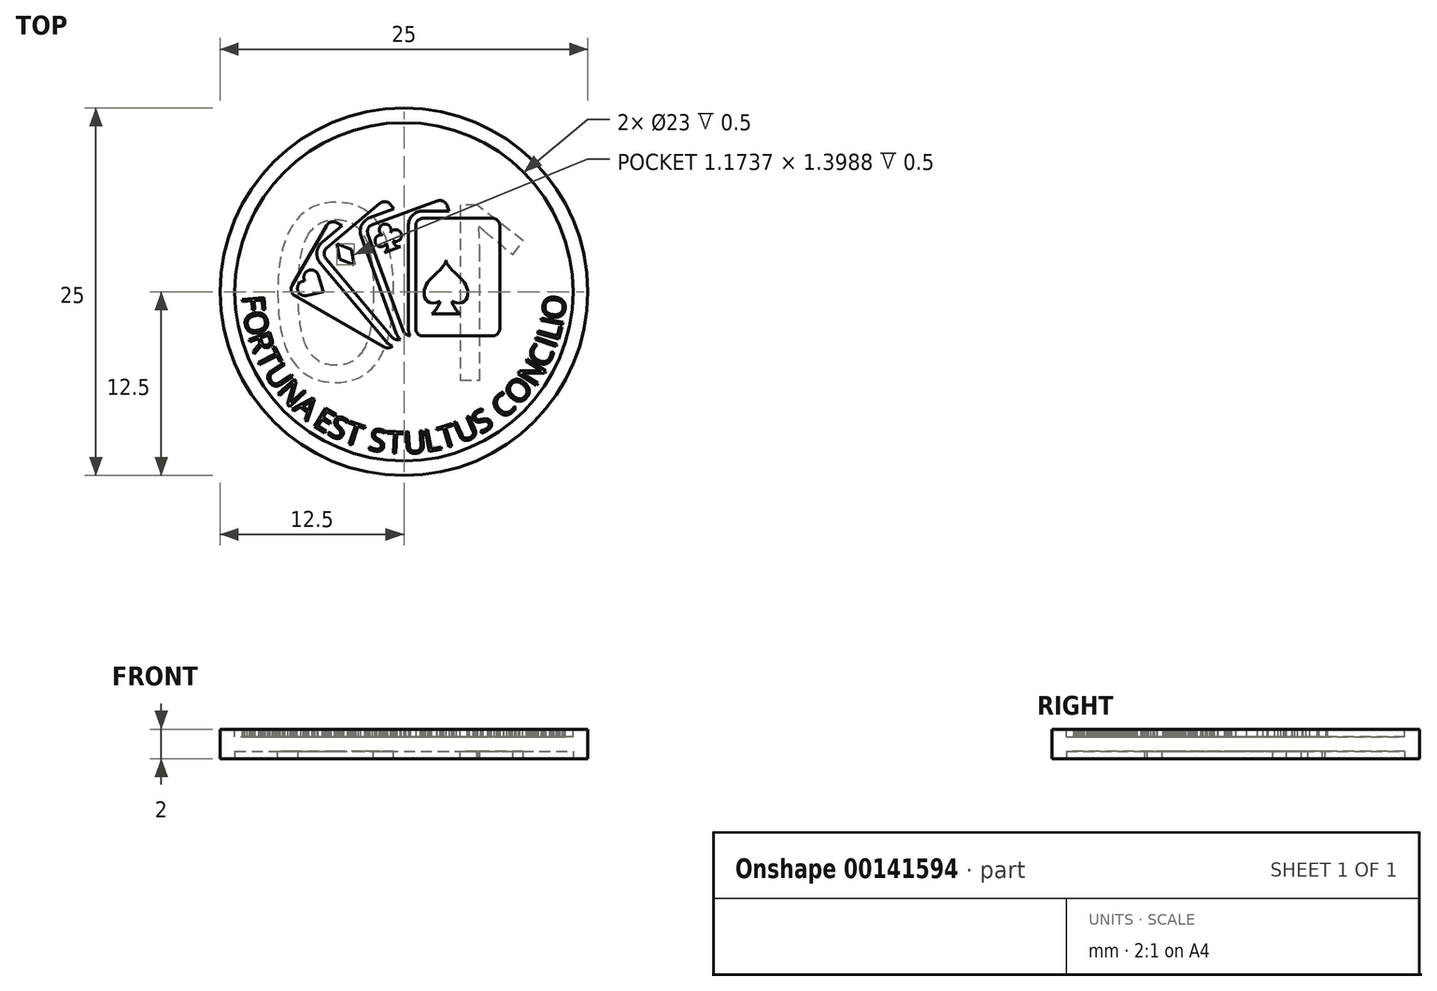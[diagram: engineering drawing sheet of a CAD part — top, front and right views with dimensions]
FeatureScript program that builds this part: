
annotation { "Feature Type Name" : "Feature", "Feature Type Description" : "" }
export const myFeature = defineFeature(function(context is Context, id is Id, definition is map)
    precondition{}
    {
        {
            assignVariable(context, id + "F0", {"name" : "ImpressionDepth", "anyValue" : 0.5});
        }
        {
            var Q0;
            Q0=qCreatedBy(makeId("Top.planeOp"),FACE);
            var sketch = newSketch(context, id + "F1", { "sketchPlane" : qUnion([Q0])});
            skCircle(sketch, "E0", {"center": v(0, 0) * mm, "radius": 12.5 * mm});
            skSolve(sketch);
        }
        {
            var Q0;
            Q0=qSketchRegion(id+"F1",true);
            extrude(context, id + "F2", {"entities" : qUnion([Q0]), "depth" : 2 * mm});
        }
        {
            var Q0;
            Q0=makeQuery(id+"F2.opExtrude","CAP_FACE",FACE,{"disambiguationData":[OSD([sQuery(id+"F1.wireOp",EDGE,"E0")])],"isStart":false});
            var sketch = newSketch(context, id + "F3", { "sketchPlane" : qUnion([Q0])});
            skCircle(sketch, "E1.0", {"center": v(0, 0) * mm, "radius": 11.5 * mm});
            skSolve(sketch);
        }
        {
            var Q0;
            Q0=qSketchRegion(id+"F3",true);
            extrude(context, id + "F4", {"entities" : qUnion([Q0]), "operationType" : NewBodyOperationType.REMOVE, "oppositeDirection" : true, "depth" : (getVariable(context, 'ImpressionDepth')) * mm});
        }
        {
            var Q0;
            Q0=makeQuery(id+"F2.opExtrude","CAP_FACE",FACE,{"disambiguationData":[OSD([sQuery(id+"F1.wireOp",EDGE,"E0")])],"isStart":true});
            var sketch = newSketch(context, id + "F5", { "sketchPlane" : qUnion([Q0])});
            skCircle(sketch, "E2.0", {"center": v(0, 0) * mm, "radius": 11.5 * mm});
            skSolve(sketch);
        }
        {
            var Q0;
            Q0=qSketchRegion(id+"F5",true);
            extrude(context, id + "F6", {"entities" : qUnion([Q0]), "operationType" : NewBodyOperationType.REMOVE, "oppositeDirection" : true, "depth" : (getVariable(context, 'ImpressionDepth')) * mm});
        }
        {
            var Q0;
            Q0=makeQuery(id+"F6.boolean.opBoolean","COPY",FACE,{"derivedFrom":makeQuery(id+"F6.opExtrude","CAP_FACE",FACE,{"disambiguationData":[OSD([sQuery(id+"F5.wireOp",EDGE,"E2.0")])],"isStart":false})});
            var sketch = newSketch(context, id + "F7", { "sketchPlane" : qUnion([Q0])});
            skText(sketch, "E3", { "text": "10", "fontName": "OpenSans-Regular.ttf"});
            skPoint(sketch, "E4", {"position": v(0, 0) * mm});
            const initialGuessF7  = {"E3": [0.00965, 0.006, -1, 0, 0.012]};
            skSetInitialGuess(sketch, initialGuessF7);
            skSolve(sketch);
        }
        {
            var Q0;
            Q0 = qSketchRegion(id + "F7", true);
            extrude(context, id + "F8", {"entities" : qUnion([Q0]), "operationType" : NewBodyOperationType.ADD, "depth" : (getVariable(context, 'ImpressionDepth')) * mm});
        }
        {
            var Q0;
            Q0=makeQuery(id+"F4.boolean.opBoolean","COPY",FACE,{"derivedFrom":makeQuery(id+"F4.opExtrude","CAP_FACE",FACE,{"disambiguationData":[OSD([sQuery(id+"F3.wireOp",EDGE,"E1.0")])],"isStart":false})});
            var sketch = newSketch(context, id + "F9", { "sketchPlane" : qUnion([Q0])});
            skLineSegment(sketch, "E5.bottom", {"start": v(1.3, 5) * mm, "end": v(6.01, 5) * mm});
            skLineSegment(sketch, "E5.top", {"start": v(1.3, -3) * mm, "end": v(6.01, -3) * mm});
            skLineSegment(sketch, "E5.left", {"start": v(0.8, 4.5) * mm, "end": v(0.8, -2.5) * mm});
            skLineSegment(sketch, "E5.right", {"start": v(6.51, 4.5) * mm, "end": v(6.51, -2.5) * mm});
            skPoint(sketch, "E6.visualSharp", {"position": v(0.8, 5) * mm});
            skArc(sketch, "E6.filletArc", {"start": v(1.3, 5) * mm, "mid": v(0.95, 4.85) * mm, "end": v(0.8, 4.5) * mm});
            skPoint(sketch, "E7.visualSharp", {"position": v(6.51, 5) * mm});
            skArc(sketch, "E7.filletArc", {"start": v(6.51, 4.5) * mm, "mid": v(6.37, 4.85) * mm, "end": v(6.01, 5) * mm});
            skPoint(sketch, "E8.visualSharp", {"position": v(0.8, -3) * mm});
            skArc(sketch, "E8.filletArc", {"start": v(0.8, -2.5) * mm, "mid": v(0.95, -2.85) * mm, "end": v(1.3, -3) * mm});
            skPoint(sketch, "E9.visualSharp", {"position": v(6.51, -3) * mm});
            skArc(sketch, "E9.filletArc", {"start": v(6.01, -3) * mm, "mid": v(6.37, -2.85) * mm, "end": v(6.51, -2.5) * mm});
            skPoint(sketch, "E10", {"position": v(0.8, -5) * mm});
            skLineSegment(sketch, "E11.bottom", {"start": v(-2.15, 4.57) * mm, "end": v(2.28, 6.18) * mm});
            skLineSegment(sketch, "E11.left", {"start": v(-2.45, 3.93) * mm, "end": v(-0.06, -2.65) * mm});
            skLineSegment(sketch, "E11.right", {"start": v(2.92, 5.88) * mm, "end": v(3.06, 5.5) * mm});
            skPoint(sketch, "E12.visualSharp", {"position": v(-2.62, 4.4) * mm});
            skArc(sketch, "E12.filletArc", {"start": v(-2.15, 4.57) * mm, "mid": v(-2.43, 4.3) * mm, "end": v(-2.45, 3.93) * mm});
            skPoint(sketch, "E13.visualSharp", {"position": v(2.75, 6.35) * mm});
            skArc(sketch, "E13.filletArc", {"start": v(2.92, 5.88) * mm, "mid": v(2.66, 6.16) * mm, "end": v(2.28, 6.18) * mm});
            skPoint(sketch, "E14.visualSharp", {"position": v(0.12, -3.12) * mm});
            skArc(sketch, "E14.filletArc", {"start": v(-0.06, -2.65) * mm, "mid": v(0.13, -2.9) * mm, "end": v(0.42, -2.98) * mm});
            skLineSegment(sketch, "E15", {"start": v(0.8, -5) * mm, "end": v(-2.62, 4.4) * mm, "construction": true});
            skLineSegment(sketch, "E16", {"start": v(0.8, -3) * mm, "end": v(0.8, -5) * mm, "construction": true});
            skLineSegment(sketch, "E17", {"start": v(1.3, 5) * mm, "end": v(3.24, 5) * mm});
            skArc(sketch, "E18.0", {"start": v(0.3, -2.5) * mm, "mid": v(0.33, -2.75) * mm, "end": v(0.42, -2.98) * mm});
            skLineSegment(sketch, "E18.1", {"start": v(0.3, 4.5) * mm, "end": v(0.3, -2.5) * mm});
            skArc(sketch, "E18.2", {"start": v(1.3, 5.5) * mm, "mid": v(0.6, 5.2) * mm, "end": v(0.3, 4.5) * mm});
            skLineSegment(sketch, "E18.3", {"start": v(1.3, 5.5) * mm, "end": v(3.06, 5.5) * mm});
            skLineSegment(sketch, "E19", {"start": v(-0.06, -2.65) * mm, "end": v(0.41, -2.48) * mm, "construction": true});
            skLineSegment(sketch, "E20", {"start": v(0.42, -2.98) * mm, "end": v(0.41, -2.48) * mm, "construction": true});
            skLineSegment(sketch, "E21.bottom", {"start": v(-5.24, 2.98) * mm, "end": v(-1.63, 6.01) * mm});
            skLineSegment(sketch, "E21.left", {"start": v(-5.3, 2.28) * mm, "end": v(-0.8, -3.08) * mm});
            skLineSegment(sketch, "E21.right", {"start": v(-0.93, 5.95) * mm, "end": v(-0.67, 5.64) * mm});
            skPoint(sketch, "E22.visualSharp", {"position": v(-5.63, 2.66) * mm});
            skArc(sketch, "E22.filletArc", {"start": v(-5.24, 2.98) * mm, "mid": v(-5.42, 2.64) * mm, "end": v(-5.3, 2.28) * mm});
            skPoint(sketch, "E23.visualSharp", {"position": v(-1.25, 6.33) * mm});
            skArc(sketch, "E23.filletArc", {"start": v(-0.93, 5.95) * mm, "mid": v(-1.27, 6.13) * mm, "end": v(-1.63, 6.01) * mm});
            skPoint(sketch, "E24.visualSharp", {"position": v(-0.49, -3.47) * mm});
            skArc(sketch, "E24.filletArc", {"start": v(-0.8, -3.08) * mm, "mid": v(-0.55, -3.25) * mm, "end": v(-0.25, -3.23) * mm});
            skLineSegment(sketch, "E25", {"start": v(-0.49, -3.47) * mm, "end": v(0.8, -5) * mm, "construction": true});
            skLineSegment(sketch, "E26", {"start": v(-5.24, 2.98) * mm, "end": v(-2.54, 5.26) * mm});
            skArc(sketch, "E27.0", {"start": v(-0.52, -2.82) * mm, "mid": v(-0.41, -3.04) * mm, "end": v(-0.25, -3.23) * mm});
            skLineSegment(sketch, "E27.1", {"start": v(-2.92, 3.76) * mm, "end": v(-0.52, -2.82) * mm});
            skArc(sketch, "E27.2", {"start": v(-2.32, 5.04) * mm, "mid": v(-2.89, 4.52) * mm, "end": v(-2.92, 3.76) * mm});
            skLineSegment(sketch, "E27.3", {"start": v(-2.32, 5.04) * mm, "end": v(-0.67, 5.64) * mm});
            skLineSegment(sketch, "E28", {"start": v(-0.8, -3.08) * mm, "end": v(-0.42, -2.76) * mm, "construction": true});
            skLineSegment(sketch, "E29", {"start": v(-0.25, -3.23) * mm, "end": v(-0.42, -2.76) * mm, "construction": true});
            skLineSegment(sketch, "E30.bottom", {"start": v(-7.61, 0.43) * mm, "end": v(-5.25, 4.52) * mm});
            skLineSegment(sketch, "E30.top", {"start": v(-0.4, -3.07) * mm, "end": v(-0.34, -2.98) * mm});
            skLineSegment(sketch, "E30.left", {"start": v(-7.43, -0.25) * mm, "end": v(-1.37, -3.75) * mm});
            skLineSegment(sketch, "E30.right", {"start": v(-4.57, 4.7) * mm, "end": v(-4.22, 4.5) * mm});
            skPoint(sketch, "E31.visualSharp", {"position": v(-7.86, 0) * mm});
            skArc(sketch, "E31.filletArc", {"start": v(-7.61, 0.43) * mm, "mid": v(-7.66, 0.05) * mm, "end": v(-7.43, -0.25) * mm});
            skPoint(sketch, "E32.visualSharp", {"position": v(-5, 4.95) * mm});
            skArc(sketch, "E32.filletArc", {"start": v(-4.57, 4.7) * mm, "mid": v(-4.95, 4.75) * mm, "end": v(-5.25, 4.52) * mm});
            skPoint(sketch, "E33.visualSharp", {"position": v(-0.93, -4) * mm});
            skArc(sketch, "E33.filletArc", {"start": v(-1.37, -3.75) * mm, "mid": v(-1.07, -3.81) * mm, "end": v(-0.79, -3.7) * mm});
            skPoint(sketch, "E34.visualSharp", {"position": v(1.93, 0.95) * mm});
            skLineSegment(sketch, "E35", {"start": v(-0.93, -4) * mm, "end": v(0.8, -5) * mm, "construction": true});
            skLineSegment(sketch, "E36", {"start": v(-7.61, 0.43) * mm, "end": v(-5.67, 3.8) * mm});
            skLineSegment(sketch, "E37.0", {"start": v(-5.57, 3.36) * mm, "end": v(-4.22, 4.5) * mm});
            skArc(sketch, "E37.1", {"start": v(-5.57, 3.36) * mm, "mid": v(-5.92, 2.69) * mm, "end": v(-5.69, 1.96) * mm});
            skLineSegment(sketch, "E37.2", {"start": v(-5.69, 1.96) * mm, "end": v(-1.19, -3.4) * mm});
            skArc(sketch, "E37.3", {"start": v(-1.19, -3.4) * mm, "mid": v(-1, -3.58) * mm, "end": v(-0.79, -3.7) * mm});
            skSolve(sketch);
        }
        {
            var Q0;
            Q0 = qSketchRegion(id + "F9", true);
            extrude(context, id + "F10", {"entities" : qUnion([Q0]), "operationType" : NewBodyOperationType.ADD, "depth" : (getVariable(context, 'ImpressionDepth')) * mm});
        }
        {
            var Q0;
            Q0=makeQuery(id+"F10.opExtrude","CAP_FACE",FACE,{"disambiguationData":[OSD([sQuery(id+"F9.wireOp",EDGE,"E5.bottom"),sQuery(id+"F9.wireOp",EDGE,"E5.top"),sQuery(id+"F9.wireOp",EDGE,"E5.right"),sQuery(id+"F9.wireOp",EDGE,"E6.filletArc"),sQuery(id+"F9.wireOp",EDGE,"E7.filletArc"),sQuery(id+"F9.wireOp",EDGE,"E8.filletArc"),sQuery(id+"F9.wireOp",EDGE,"E9.filletArc"),sQuery(id+"F9.wireOp",EDGE,"E17"),sQuery(id+"F9.wireOp",EDGE,"E5.left")])],"isStart":false});
            var sketch = newSketch(context, id + "F11", { "sketchPlane" : qUnion([Q0])});
            skLineSegment(sketch, "E38", {"start": v(2.86, 5) * mm, "end": v(2.86, -3) * mm, "construction": true});
            skLineSegment(sketch, "E39", {"start": v(0.8, 0) * mm, "end": v(6.51, 0) * mm, "construction": true});
            skLineSegment(sketch, "E40", {"start": v(2.86, -1.5) * mm, "end": v(3.82, -1.5) * mm});
            skPoint(sketch, "E41", {"position": v(3.26, -0.64) * mm});
            skPoint(sketch, "E42", {"position": v(4.73, -0.3) * mm});
            skArc(sketch, "E43", {"start": v(3.26, -0.64) * mm, "mid": v(3.46, -1.12) * mm, "end": v(3.82, -1.5) * mm});
            skPoint(sketch, "E44", {"position": v(2.86, 2.16) * mm});
            skPoint(sketch, "E45", {"position": v(3.36, 1.4) * mm});
            skPoint(sketch, "E46", {"position": v(4.16, 0.53) * mm});
            skFitSpline(sketch, "E47", {"points": [v(3.26, -0.64) * mm, v(4.29, -0.43) * mm, v(4.16, 0.53) * mm, v(3.36, 1.4) * mm, v(2.86, 2.16) * mm], "startDerivative": vector(6.48, -2.91) * mm, "endDerivative": vector(0, 2.74) * mm});
            skFitSpline(sketch, "E48.MirrorCS", {"points": [v(2.46, -0.64) * mm, v(1.43, -0.43) * mm, v(1.56, 0.53) * mm, v(2.36, 1.4) * mm, v(2.86, 2.16) * mm], "startDerivative": vector(-6.48, -2.91) * mm, "endDerivative": vector(0, 2.74) * mm});
            skArc(sketch, "E49.MirrorCS", {"start": v(2.46, -0.64) * mm, "mid": v(2.25, -1.12) * mm, "end": v(1.9, -1.5) * mm});
            skLineSegment(sketch, "E50.MirrorCS", {"start": v(2.86, -1.5) * mm, "end": v(1.9, -1.5) * mm});
            skLineSegment(sketch, "E51", {"start": v(-2.14, 3.08) * mm, "end": v(-1.01, 3.5) * mm, "construction": true});
            skLineSegment(sketch, "E52", {"start": v(-1.01, 3.5) * mm, "end": v(-1.5, 4.8) * mm, "construction": true});
            skLineSegment(sketch, "E53", {"start": v(-1.01, 3.5) * mm, "end": v(-0.53, 2.18) * mm, "construction": true});
            skLineSegment(sketch, "E54", {"start": v(-0.79, 2.87) * mm, "end": v(-0.25, 3.06) * mm});
            skPoint(sketch, "E55", {"position": v(-0.73, 3.46) * mm});
            skPoint(sketch, "E56", {"position": v(-1.27, 4.2) * mm});
            skPoint(sketch, "E57", {"position": v(-0.57, 3.83) * mm});
            skPoint(sketch, "E58", {"position": v(-0.29, 3.5) * mm});
            skArc(sketch, "E59", {"start": v(-0.73, 3.46) * mm, "mid": v(-0.57, 3.16) * mm, "end": v(-0.25, 3.06) * mm});
            skArc(sketch, "E60", {"start": v(-0.73, 3.46) * mm, "mid": v(-0.19, 3.95) * mm, "end": v(-0.91, 4.04) * mm});
            skArc(sketch, "E61", {"start": v(-1.41, 4.58) * mm, "mid": v(-0.98, 4.48) * mm, "end": v(-0.91, 4.04) * mm});
            skArc(sketch, "E62.MirrorCS", {"start": v(-1.41, 4.58) * mm, "mid": v(-1.67, 4.22) * mm, "end": v(-1.44, 3.84) * mm});
            skArc(sketch, "E63.MirrorCS", {"start": v(-1.2, 3.29) * mm, "mid": v(-1.94, 3.3) * mm, "end": v(-1.44, 3.84) * mm});
            skArc(sketch, "E64.MirrorCS", {"start": v(-1.2, 3.29) * mm, "mid": v(-1.14, 2.96) * mm, "end": v(-1.32, 2.67) * mm});
            skLineSegment(sketch, "E65.MirrorCS", {"start": v(-0.79, 2.87) * mm, "end": v(-1.32, 2.67) * mm});
            skLineSegment(sketch, "E66", {"start": v(-4.89, 1.78) * mm, "end": v(-3.97, 2.55) * mm, "construction": true});
            skLineSegment(sketch, "E67", {"start": v(-3.97, 2.55) * mm, "end": v(-4.7, 3.43) * mm, "construction": true});
            skLineSegment(sketch, "E68", {"start": v(-4.35, 2.23) * mm, "end": v(-4.55, 3.25) * mm});
            skLineSegment(sketch, "E69", {"start": v(-3.97, 2.55) * mm, "end": v(-3.38, 1.85) * mm, "construction": true});
            skLineSegment(sketch, "E70", {"start": v(-4.35, 2.23) * mm, "end": v(-3.38, 1.85) * mm});
            skLineSegment(sketch, "E71.MirrorCS", {"start": v(-3.58, 2.87) * mm, "end": v(-4.55, 3.25) * mm});
            skLineSegment(sketch, "E72.MirrorCS", {"start": v(-3.58, 2.87) * mm, "end": v(-3.38, 1.85) * mm});
            skLineSegment(sketch, "E73", {"start": v(-6.86, -0.58) * mm, "end": v(-6.26, 0.46) * mm, "construction": true});
            skLineSegment(sketch, "E74", {"start": v(-6.26, 0.46) * mm, "end": v(-7.26, 1.04) * mm, "construction": true});
            skLineSegment(sketch, "E75", {"start": v(-6.26, 0.46) * mm, "end": v(-5.47, 0) * mm, "construction": true});
            skLineSegment(sketch, "E76", {"start": v(-5.47, 0) * mm, "end": v(-5.83, 1.14) * mm});
            skArc(sketch, "E77", {"start": v(-5.83, 1.14) * mm, "mid": v(-6.5, 1.45) * mm, "end": v(-6.74, 0.74) * mm});
            skArc(sketch, "E78.MirrorCS", {"start": v(-6.63, -0.25) * mm, "mid": v(-7.24, 0.19) * mm, "end": v(-6.74, 0.74) * mm});
            skLineSegment(sketch, "E79.MirrorCS", {"start": v(-5.47, 0) * mm, "end": v(-6.63, -0.25) * mm});
            skSolve(sketch);
        }
        {
            var Q0;
            Q0 = qSketchRegion(id + "F11", true);
            extrude(context, id + "F12", {"entities" : qUnion([Q0]), "operationType" : NewBodyOperationType.REMOVE, "oppositeDirection" : true, "depth" : (getVariable(context, 'ImpressionDepth')) * mm});
        }
        {
            var Q0;
            Q0=makeQuery(id+"F4.boolean.opBoolean","COPY",FACE,{"derivedFrom":makeQuery(id+"F4.opExtrude","CAP_FACE",FACE,{"disambiguationData":[OSD([sQuery(id+"F3.wireOp",EDGE,"E1.0")])],"isStart":false})});
            var sketch = newSketch(context, id + "F13", { "sketchPlane" : qUnion([Q0])});
            skCircle(sketch, "E80", {"center": v(0, 0) * mm, "radius": 11 * mm, "construction": true});
            skLineSegment(sketch, "E81", {"start": v(0, 0) * mm, "end": v(0, -11) * mm, "construction": true});
            skText(sketch, "E82", { "text": "U", "fontName": "OpenSans-Regular.ttf"});
            skText(sketch, "E83", { "text": "L\n", "fontName": "OpenSans-Regular.ttf"});
            skText(sketch, "E84", { "text": "T", "fontName": "OpenSans-Regular.ttf"});
            skText(sketch, "E85", { "text": "U", "fontName": "OpenSans-Regular.ttf"});
            skText(sketch, "E86", { "text": "S", "fontName": "OpenSans-Regular.ttf"});
            skText(sketch, "E87", { "text": "C", "fontName": "OpenSans-Regular.ttf"});
            skText(sketch, "E88", { "text": "O", "fontName": "OpenSans-Regular.ttf"});
            skText(sketch, "E89", { "text": "N", "fontName": "OpenSans-Regular.ttf"});
            skText(sketch, "E90", { "text": "C", "fontName": "OpenSans-Regular.ttf"});
            skText(sketch, "E91", { "text": "O", "fontName": "OpenSans-Regular.ttf"});
            skText(sketch, "E92", { "text": "I", "fontName": "OpenSans-Regular.ttf"});
            skText(sketch, "E93", { "text": "L", "fontName": "OpenSans-Regular.ttf"});
            skText(sketch, "E94", { "text": "I", "fontName": "OpenSans-Regular.ttf"});
            skText(sketch, "E95", { "text": "F", "fontName": "OpenSans-Regular.ttf"});
            skText(sketch, "E96", { "text": "O", "fontName": "OpenSans-Regular.ttf"});
            skText(sketch, "E97", { "text": "R", "fontName": "OpenSans-Regular.ttf"});
            skText(sketch, "E98", { "text": "T", "fontName": "OpenSans-Regular.ttf"});
            skText(sketch, "E99", { "text": "U", "fontName": "OpenSans-Regular.ttf"});
            skText(sketch, "E100", { "text": "N", "fontName": "OpenSans-Regular.ttf"});
            skText(sketch, "E101", { "text": "A", "fontName": "OpenSans-Regular.ttf"});
            skText(sketch, "E102", { "text": "E", "fontName": "OpenSans-Regular.ttf"});
            skText(sketch, "E103", { "text": "S", "fontName": "OpenSans-Regular.ttf"});
            skText(sketch, "E104", { "text": "T", "fontName": "OpenSans-Regular.ttf"});
            skText(sketch, "E105", { "text": "S", "fontName": "OpenSans-Regular.ttf"});
            skText(sketch, "E106", { "text": "T", "fontName": "OpenSans-Regular.ttf"});
            const initialGuessF13  = {"E82": [4e-05, -0.01102, 0.99756, 0.06976, 0.0015], "E83": [0.00153, -0.0109, 0.98163, 0.1908, 0.0015], "E84": [0.00261, -0.0107, 0.95629, 0.29243, 0.0015], "E85": [0.00382, -0.01034, 0.9129, 0.40819, 0.0015], "E86": [0.00521, -0.0097, 0.85425, 0.51986, 0.0015], "E87": [0.00674, -0.00872, 0.751, 0.6603, 0.0015], "E88": [0.0078, -0.0078, 0.65346, 0.75696, 0.0015], "E89": [0.0089, -0.00652, 0.5351, 0.8448, 0.0015], "E90": [0.0097, -0.00525, 0.41965, 0.90769, 0.0015], "E91": [0.01086, -0.00193, 0.10138, 0.99485, 0.0015], "E92": [0.01028, -0.00393, 0.33522, 0.94214, 0.0015], "E93": [0.01048, -0.0034, 0.25807, 0.96613, 0.0015], "E94": [0.01073, -0.00244, 0.1986, 0.98008, 0.0015], "E95": [-0.01101, -0.0003, 0.07969, -0.99682, 0.0015], "E96": [-0.01093, -0.00148, 0.20736, -0.97826, 0.0015], "E97": [-0.0106, -0.00305, 0.33662, -0.94164, 0.0015], "E98": [-0.01012, -0.00436, 0.4478, -0.89413, 0.0015], "E99": [-0.00955, -0.0055, 0.55578, -0.83133, 0.0015], "E100": [-0.00869, -0.00679, 0.66797, -0.74419, 0.0015], "E101": [-0.0076, -0.00799, 0.76846, -0.6399, 0.0015], "E102": [-0.00626, -0.00906, 0.8518, -0.52386, 0.0015], "E103": [-0.00527, -0.00967, 0.90245, -0.43079, 0.0015], "E104": [-0.00418, -0.0102, 0.94569, -0.32507, 0.0015], "E105": [-0.00247, -0.01073, 0.98509, -0.17205, 0.0015], "E106": [-0.00121, -0.01095, 0.9986, -0.05274, 0.0015]};
            skSetInitialGuess(sketch, initialGuessF13);
            skSolve(sketch);
        }
        {
            var Q0;
            Q0 = qSketchRegion(id + "F13", true);
            extrude(context, id + "F14", {"entities" : qUnion([Q0]), "operationType" : NewBodyOperationType.ADD, "depth" : (getVariable(context, 'ImpressionDepth')) * mm});
        }
    });
